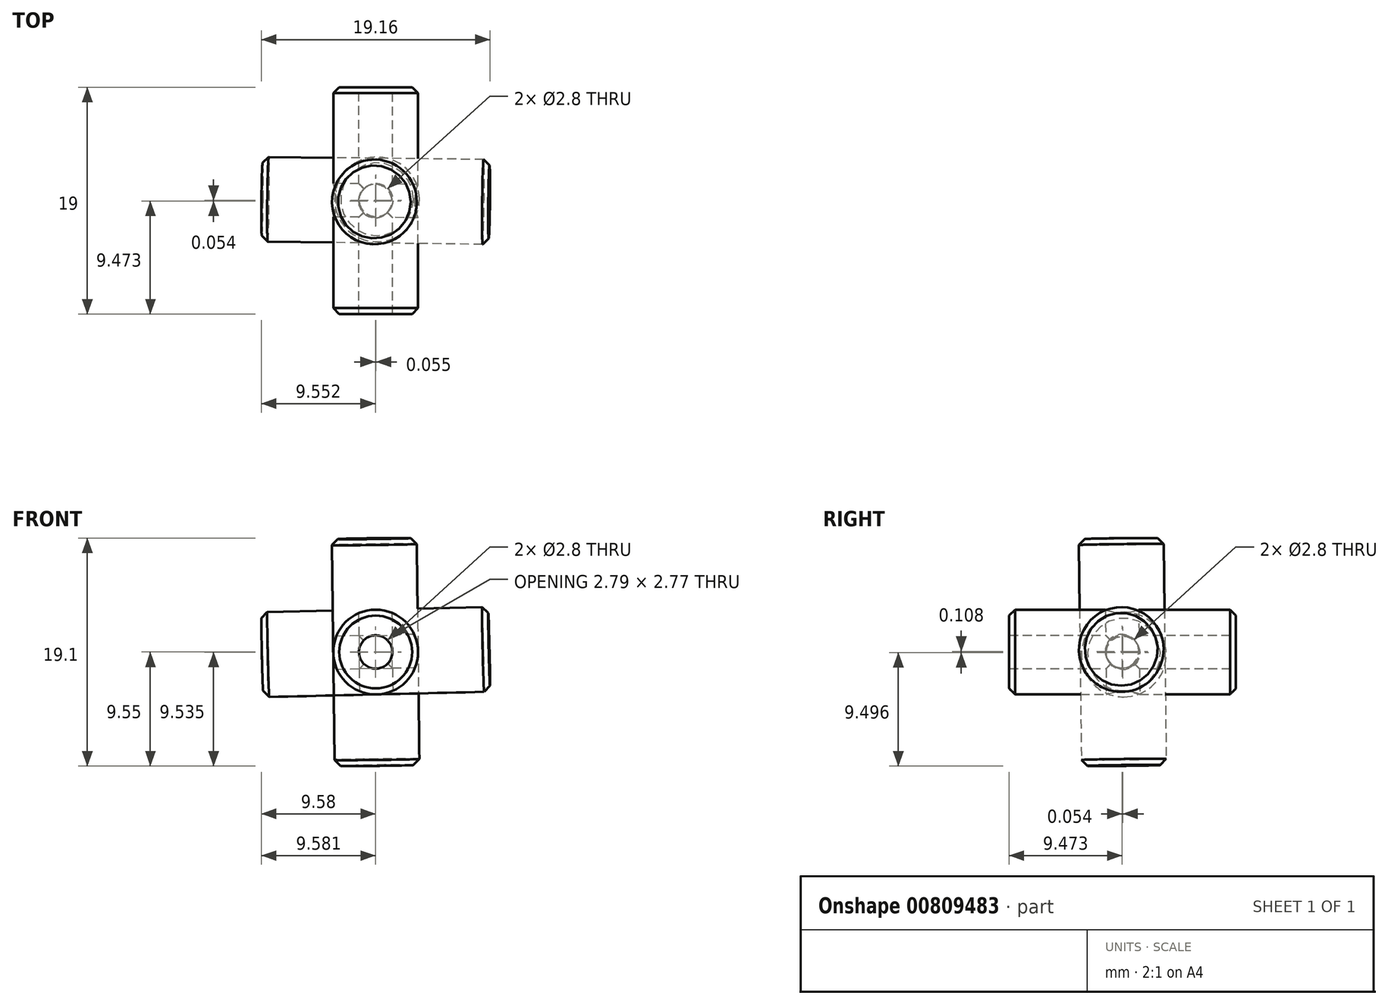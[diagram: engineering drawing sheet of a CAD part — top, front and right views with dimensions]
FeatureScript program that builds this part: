
annotation { "Feature Type Name" : "Feature", "Feature Type Description" : "" }
export const myFeature = defineFeature(function(context is Context, id is Id, definition is map)
    precondition{}
    {
        {
            var Q0;
            Q0=qCreatedBy(makeId("Front.planeOp"),FACE);
            var sketch = newSketch(context, id + "F0", { "sketchPlane" : qUnion([Q0])});
            skCircle(sketch, "E0", {"center": v(0, 0) * mm, "radius": 3.55 * mm});
            skSolve(sketch);
        }
        {
            var Q0;
            Q0 = qSketchRegion(id + "F0", true);
            extrude(context, id + "F1", {"entities" : qUnion([Q0]), "endBound" : BoundingType.SYMMETRIC, "depth" : 19 * mm, "offsetDistance" : 25 * mm});
        }
        {
            var Q0;
            Q0=qCreatedBy(makeId("Front.planeOp"),FACE);
            var sketch = newSketch(context, id + "F2", { "sketchPlane" : qUnion([Q0])});
            skCircle(sketch, "E1", {"center": v(0, 0) * mm, "radius": 1.4 * mm});
            skSolve(sketch);
        }
        {
            var Q0;
            Q0 = qSketchRegion(id + "F2", true);
            extrude(context, id + "F3", {"entities" : qUnion([Q0]), "endBound" : BoundingType.SYMMETRIC, "depth" : 20 * mm, "offsetDistance" : 25 * mm});
        }
        {
            var Q0;
            Q0=qCreatedBy(makeId("Front.planeOp"),FACE);
            var sketch = newSketch(context, id + "F4", { "sketchPlane" : qUnion([Q0])});
            skLineSegment(sketch, "E2.bottom", {"start": v(0, 0) * mm, "end": v(9.65, 0) * mm});
            skLineSegment(sketch, "E2.top", {"start": v(0, 10) * mm, "end": v(9.65, 10) * mm});
            skLineSegment(sketch, "E2.left", {"start": v(0, 0) * mm, "end": v(0, 10) * mm});
            skLineSegment(sketch, "E2.right", {"start": v(9.65, 0) * mm, "end": v(9.65, 10) * mm});
            skSolve(sketch);
        }
        {
            var Q0;
            Q0 = qSketchRegion(id + "F4", true);
            extrude(context, id + "F5", {"entities" : qUnion([Q0]), "depth" : 10 * mm, "offsetDistance" : 25 * mm});
        }
        {
            var Q0;
            Q0=qCreatedBy(makeId("Origin.pointOp"),VERTEX);
            var Q1;
            Q1=makeQuery(id+"F5.opExtrude","CAP_VERTEX",VERTEX,{"disambiguationData":[OSD([sQuery(id+"F4.wireOp",EDGE,"E2.top"),sQuery(id+"F4.wireOp",EDGE,"E2.right")])],"isStart":false});
            var Q2;
            Q2=makeQuery(id+"F5.opExtrude","CAP_VERTEX",VERTEX,{"disambiguationData":[OSD([sQuery(id+"F4.wireOp",EDGE,"E2.bottom"),sQuery(id+"F4.wireOp",EDGE,"E2.right")])],"isStart":false});
            cPlane(context, id + "F6", {"entities" : qUnion([Q0, Q1, Q2]), "cplaneType" : CPlaneType.THREE_POINT, "offset" : 25 * mm, "width" : 150 * mm, "height" : 150 * mm});
        }
        {
            var Q0;
            Q0=qCreatedBy(id+"F6.planeOp",FACE);
            var sketch = newSketch(context, id + "F7", { "sketchPlane" : qUnion([Q0])});
            skLineSegment(sketch, "E3", {"start": v(0, 0) * mm, "end": v(13.9, 10) * mm});
            skSolve(sketch);
        }
        {
            var Q0;
            Q0=makeQuery(id+"F5.opExtrude","SWEPT_BODY",BODY,{"disambiguationData":[OSD([sQuery(id+"F4.wireOp",EDGE,"E2.bottom"),sQuery(id+"F4.wireOp",EDGE,"E2.top"),sQuery(id+"F4.wireOp",EDGE,"E2.left"),sQuery(id+"F4.wireOp",EDGE,"E2.right")])]});
            deleteBodies(context, id + "F8", {"entities" : qUnion([Q0])});
        }
        {
            var Q0;
            Q0=makeQuery(id+"F3.opExtrude","SWEPT_BODY",BODY,{"disambiguationData":[OSD([sQuery(id+"F2.wireOp",EDGE,"E1")])]});
            var Q1;
            Q1=makeQuery(id+"F1.opExtrude","SWEPT_BODY",BODY,{"disambiguationData":[OSD([sQuery(id+"F0.wireOp",EDGE,"E0")])]});
            var Q2;
            Q2=sQuery(id+"F7.wireOp",EDGE,"E3");
            circularPattern(context, id + "F9", {"entities" : qUnion([Q0, Q1]), "axis" : qUnion([Q2]), "angle" : 360 * degree, "instanceCount" : 3, "equalSpace" : true});
        }
        {
            var Q0;
            Q0=makeQuery(id+"F9.opPattern","COPY",BODY,{"derivedFrom":makeQuery(id+"F3.opExtrude","SWEPT_BODY",BODY,{"disambiguationData":[OSD([sQuery(id+"F2.wireOp",EDGE,"E1")])]}),"instanceName":"1"});
            var Q1;
            Q1=makeQuery(id+"F9.opPattern","COPY",BODY,{"derivedFrom":makeQuery(id+"F3.opExtrude","SWEPT_BODY",BODY,{"disambiguationData":[OSD([sQuery(id+"F2.wireOp",EDGE,"E1")])]}),"instanceName":"2"});
            var Q2;
            Q2=makeQuery(id+"F3.opExtrude","SWEPT_BODY",BODY,{"disambiguationData":[OSD([sQuery(id+"F2.wireOp",EDGE,"E1")])]});
            var Q3;
            Q3=makeQuery(id+"F1.opExtrude","SWEPT_BODY",BODY,{"disambiguationData":[OSD([sQuery(id+"F0.wireOp",EDGE,"E0")])]});
            booleanBodies(context, id + "F10", {"operationType" : BooleanOperationType.SUBTRACTION, "tools" : qUnion([Q0, Q1, Q2]), "targets" : qUnion([Q3])});
        }
        {
            var Q0;
            Q0=makeQuery(id+"F1.opExtrude","CAP_EDGE",EDGE,{"disambiguationData":[OSD([sQuery(id+"F0.wireOp",EDGE,"E0")])],"isStart":false});
            var Q1;
            Q1=makeQuery(id+"F9.opPattern","COPY",EDGE,{"derivedFrom":makeQuery(id+"F1.opExtrude","CAP_EDGE",EDGE,{"disambiguationData":[OSD([sQuery(id+"F0.wireOp",EDGE,"E0")])],"isStart":true}),"instanceName":"1"});
            var Q2;
            Q2=makeQuery(id+"F1.opExtrude","CAP_EDGE",EDGE,{"disambiguationData":[OSD([sQuery(id+"F0.wireOp",EDGE,"E0")])],"isStart":true});
            var Q3;
            Q3=makeQuery(id+"F9.opPattern","COPY",EDGE,{"derivedFrom":makeQuery(id+"F1.opExtrude","CAP_EDGE",EDGE,{"disambiguationData":[OSD([sQuery(id+"F0.wireOp",EDGE,"E0")])],"isStart":false}),"instanceName":"1"});
            var Q4;
            Q4=makeQuery(id+"F9.opPattern","COPY",FACE,{"derivedFrom":makeQuery(id+"F1.opExtrude","CAP_FACE",FACE,{"disambiguationData":[OSD([sQuery(id+"F0.wireOp",EDGE,"E0")])],"isStart":false}),"instanceName":"2"});
            var Q5;
            Q5=makeQuery(id+"F9.opPattern","COPY",EDGE,{"derivedFrom":makeQuery(id+"F1.opExtrude","CAP_EDGE",EDGE,{"disambiguationData":[OSD([sQuery(id+"F0.wireOp",EDGE,"E0")])],"isStart":true}),"instanceName":"2"});
            chamfer(context, id + "F11", {"entities" : qUnion([Q0, Q1, Q2, Q3, Q4, Q5]), "width" : 0.5 * mm, "tangentPropagation" : true});
        }
    });
